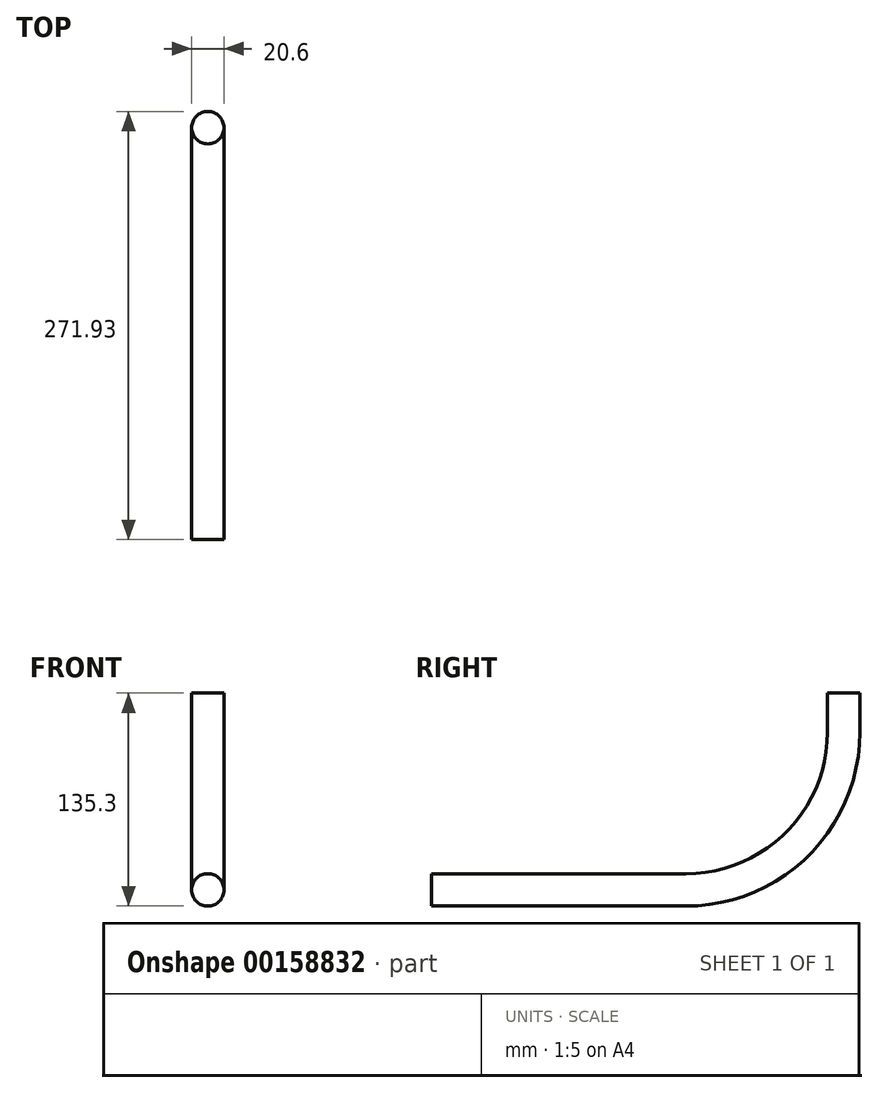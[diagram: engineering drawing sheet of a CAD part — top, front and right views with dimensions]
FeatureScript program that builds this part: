
annotation { "Feature Type Name" : "Feature", "Feature Type Description" : "" }
export const myFeature = defineFeature(function(context is Context, id is Id, definition is map)
    precondition{}
    {
        {
            var Q0;
            Q0=qCreatedBy(makeId("Right.planeOp"),FACE);
            var sketch = newSketch(context, id + "F0", { "sketchPlane" : qUnion([Q0])});
            skLineSegment(sketch, "E0", {"start": v(0, 0) * mm, "end": v(0, -25) * mm});
            skLineSegment(sketch, "E1", {"start": v(-100, -125) * mm, "end": v(-261.63, -125) * mm});
            skPoint(sketch, "E2.visualSharp", {"position": v(0, -125) * mm});
            skArc(sketch, "E2.filletArc", {"start": v(-100, -125) * mm, "mid": v(-29.29, -95.71) * mm, "end": v(0, -25) * mm});
            skSolve(sketch);
        }
        {
            var Q0;
            Q0=qCreatedBy(makeId("Top.planeOp"),FACE);
            var sketch = newSketch(context, id + "F1", { "sketchPlane" : qUnion([Q0])});
            skCircle(sketch, "E3", {"center": v(0, 0) * mm, "radius": 10.3 * mm});
            skSolve(sketch);
        }
        {
            var Q0;
            Q0=makeQuery(id+"F1.imprint","IMPRINT",FACE,{"disambiguationData":[TD([[makeQuery(id+"F1.imprint","IMPRINT",EDGE,{"derivedFrom":sQuery(id+"F1.wireOp",EDGE,"E3")}),1.0]])]});
            var Q1;
            Q1=sQuery(id+"F0.wireOp",EDGE,"E2.filletArc");
            var Q2;
            Q2=sQuery(id+"F0.wireOp",EDGE,"E0");
            var Q3;
            Q3=sQuery(id+"F0.wireOp",EDGE,"E1");
            sweep(context, id + "F2", {"profiles" : qUnion([Q0]), "path" : qUnion([Q1, Q2, Q3])});
        }
    });
